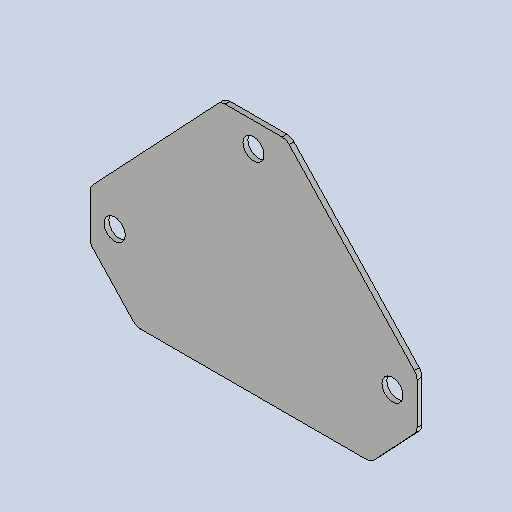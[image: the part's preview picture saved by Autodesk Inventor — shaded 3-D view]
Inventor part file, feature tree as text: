
AUTODESK INVENTOR PART (.ipt)
format: ipt  version: 2025 (Build 290162010, 162A)  size: 127,488 bytes
history: native  units: mm
features: sheet_metal_op x1, chamfer x1, sketch x1, other x1
ambient origin geometry x8: Origin, YZ Plane, XZ Plane, XY Plane, X Axis, Y Axis, Z Axis, Center Point
bodies: Solid1 (feature_tree)
feature tree (4):
  sheet_metal_op  "Face1"
  chamfer  "Corner Round2"
  sketch  "Sketch1"  dims[d2=80.0mm d3=80.0mm d6=3.0mm d17=5.0mm d18=13.0mm d19=45.0mm d20=45.0mm d21=40.0mm d22=15.0mm d23=15.0mm d24=30.0mm d25=6.0mm]
  other  "Plate1"
